# Revit family: Potentialausgleichsschiene BigBar für Industriebereich_Copper
name_source: partatom
category: Generic Models
revit_build: Autodesk Revit 2015 (Build: 20140606_1530(x64)
units: mm (PartAtom-declared; Revit-internal decimal feet)

## types (7) — shared parameters
Height = 5 mm  [stored 0.0164042 ft]
Manufacturer = OBO Bettermann
Material = Copper
URL = http://www.obo-bettermann.com
Width = 40 mm  [stored 0.131234 ft]

## per-type parameters (varying)
| type | Cut's number | GTIN | Length | Length 1 | Manufacturer Art.No. |
| 1802 5 CU | 5 | 4012195002253 | 246 mm  [stored 0.807087 ft] | 130 mm  [stored 0.426509 ft] | 5015830 |
| 1802 10 CU | 10 | 4012195002260 | 409 mm | 293 mm | 5015842 |
| 1802 6 CU | 6 | 4012195699330 | 279 mm | 163 mm | 5015832 |
| 1802 8 CU | 8 | 4012195699347 | 344 mm | 228 mm | 5015836 |
| 1802 12 CU | 12 | 4012195699354 | 474 mm | 358 mm | 5015844 |
| 1802 14 CU | 14 | 4012195699361 | 539 mm | 423 mm | 5015847 |
| 1802 20 CU | 20 | 4012195699408 | 734 mm | 618 mm | 5015849 |

note: column(s) folded — value = type name in every type: Article Type

note: [stored X ft] marks values corroborated as IEEE doubles in the binary element streams (Revit-internal decimal feet)

## geometry (parser evidence)
native form markers: Sweep x2
no freeform markers — native parametric forms only
